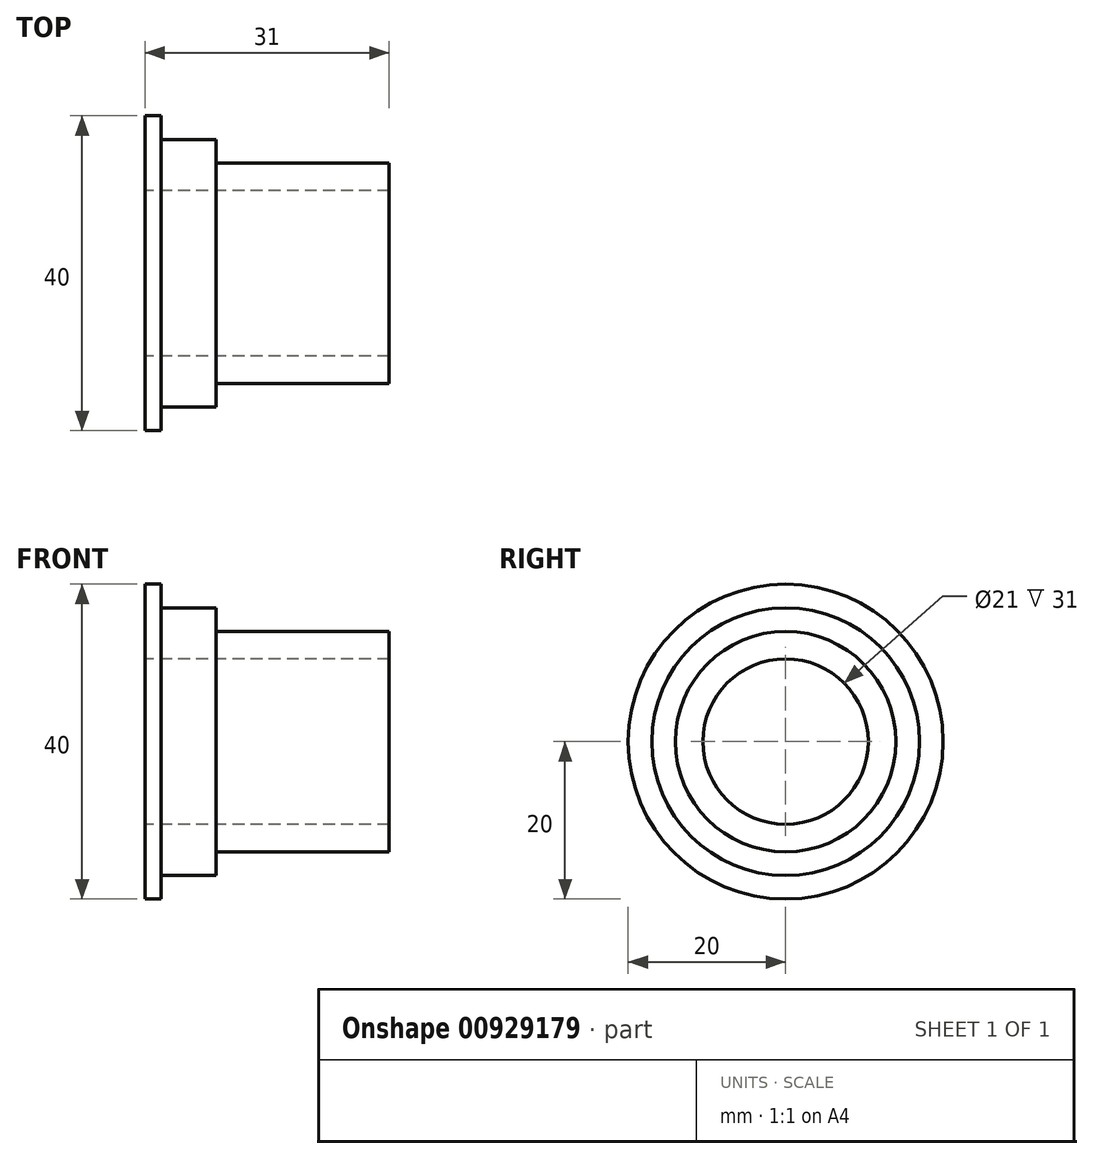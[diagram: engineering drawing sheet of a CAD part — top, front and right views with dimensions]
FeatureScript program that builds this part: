
annotation { "Feature Type Name" : "Feature", "Feature Type Description" : "" }
export const myFeature = defineFeature(function(context is Context, id is Id, definition is map)
    precondition{}
    {
        {
            var Q0;
            Q0=qCreatedBy(makeId("Top.planeOp"),FACE);
            var sketch = newSketch(context, id + "F0", { "sketchPlane" : qUnion([Q0])});
            skLineSegment(sketch, "E0", {"start": v(0, 10.5) * mm, "end": v(0, 20) * mm});
            skLineSegment(sketch, "E1", {"start": v(0, 20) * mm, "end": v(2, 20) * mm});
            skLineSegment(sketch, "E2", {"start": v(2, 20) * mm, "end": v(2, 17) * mm});
            skLineSegment(sketch, "E3", {"start": v(2, 17) * mm, "end": v(9, 17) * mm});
            skLineSegment(sketch, "E4", {"start": v(9, 17) * mm, "end": v(9, 14) * mm});
            skLineSegment(sketch, "E5", {"start": v(9, 14) * mm, "end": v(31, 14) * mm});
            skLineSegment(sketch, "E6", {"start": v(31, 14) * mm, "end": v(31, 10.5) * mm});
            skLineSegment(sketch, "E7", {"start": v(-19.35, 0) * mm, "end": v(53.14, 0) * mm, "construction": true});
            skLineSegment(sketch, "E8", {"start": v(0, 10.5) * mm, "end": v(31, 10.5) * mm});
            skPoint(sketch, "E9.orphan", {"position": v(31, 0) * mm});
            skSolve(sketch);
        }
        {
            var Q0;
            Q0=makeQuery(id+"F0.imprint","IMPRINT",FACE,{"disambiguationData":[TD([[makeQuery(id+"F0.imprint","IMPRINT",EDGE,{"derivedFrom":sQuery(id+"F0.wireOp",EDGE,"E0")}),-1.0]])]});
            var Q1;
            Q1=sQuery(id+"F0.wireOp",EDGE,"E7");
            revolve(context, id + "F1", {"surfaceOperationType" : NewSurfaceOperationType.NEW, "entities" : qUnion([Q0]), "axis" : qUnion([Q1]), "revolveType" : RevolveType.FULL});
        }
    });
